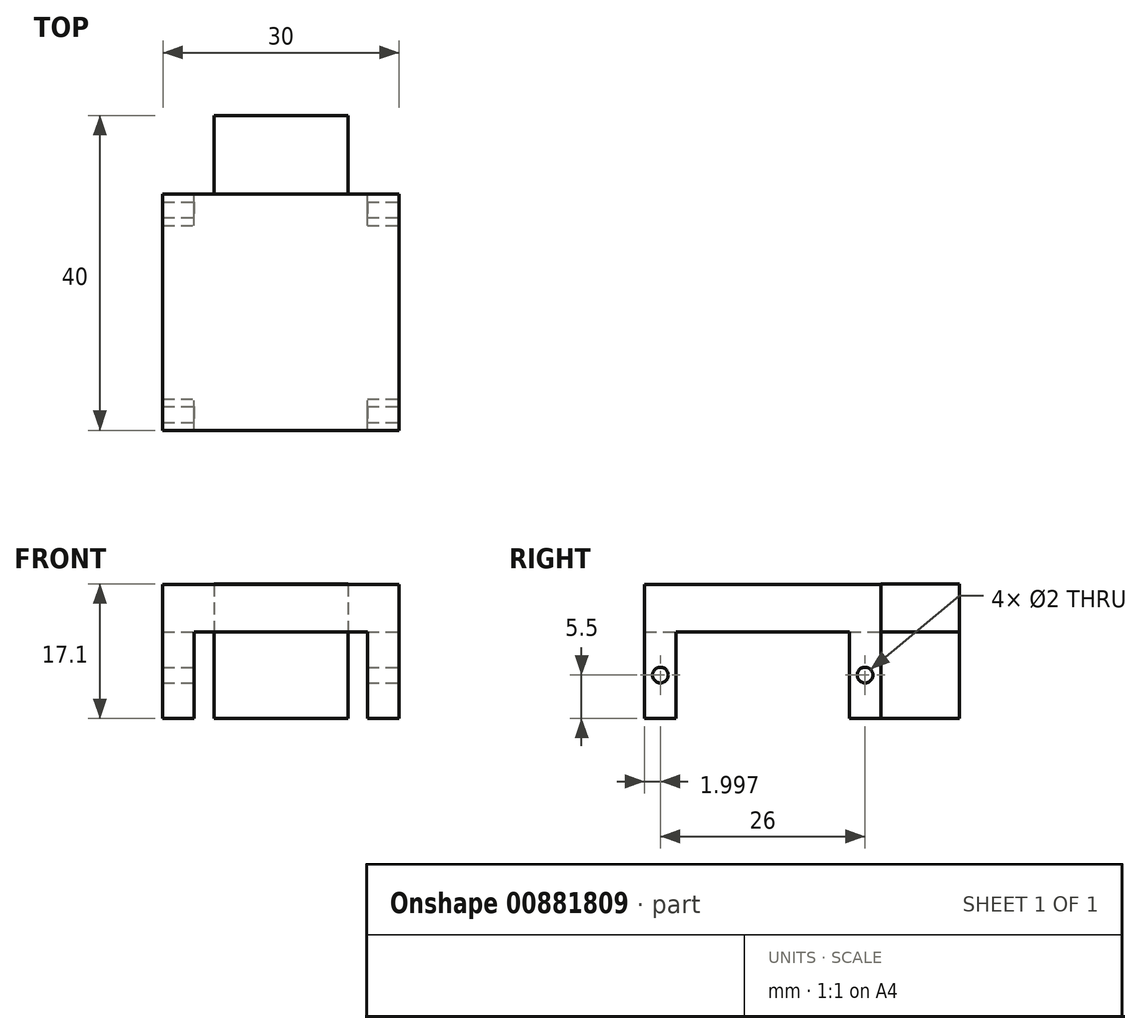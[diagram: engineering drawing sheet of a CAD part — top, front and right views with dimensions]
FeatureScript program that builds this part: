
annotation { "Feature Type Name" : "Feature", "Feature Type Description" : "" }
export const myFeature = defineFeature(function(context is Context, id is Id, definition is map)
    precondition{}
    {
        {
            var Q0;
            Q0=qCreatedBy(makeId("Top.planeOp"),FACE);
            var sketch = newSketch(context, id + "F0", { "sketchPlane" : qUnion([Q0])});
            skLineSegment(sketch, "E0.bottom", {"start": v(-18.4, 12.33) * mm, "end": v(11.6, 12.33) * mm});
            skLineSegment(sketch, "E0.top", {"start": v(-18.4, -17.67) * mm, "end": v(11.6, -17.67) * mm});
            skLineSegment(sketch, "E0.left", {"start": v(-18.4, 12.33) * mm, "end": v(-18.4, -17.67) * mm});
            skLineSegment(sketch, "E0.right", {"start": v(11.6, 12.33) * mm, "end": v(11.6, -17.67) * mm});
            skSolve(sketch);
        }
        {
            var Q0;
            Q0 = qSketchRegion(id + "F0", true);
            extrude(context, id + "F1", {"entities" : qUnion([Q0]), "depth" : 6 * mm, "offsetDistance" : 25 * mm});
        }
        {
            var Q0;
            Q0=makeQuery(id+"F1.opExtrude","CAP_FACE",FACE,{"disambiguationData":[OSD([sQuery(id+"F0.wireOp",EDGE,"E0.bottom"),sQuery(id+"F0.wireOp",EDGE,"E0.top"),sQuery(id+"F0.wireOp",EDGE,"E0.left"),sQuery(id+"F0.wireOp",EDGE,"E0.right")])],"isStart":true});
            var sketch = newSketch(context, id + "F2", { "sketchPlane" : qUnion([Q0])});
            skLineSegment(sketch, "E1.bottom", {"start": v(-18.4, 17.67) * mm, "end": v(-14.4, 17.67) * mm});
            skLineSegment(sketch, "E1.top", {"start": v(-18.4, 13.67) * mm, "end": v(-14.4, 13.67) * mm});
            skLineSegment(sketch, "E1.left", {"start": v(-18.4, 17.67) * mm, "end": v(-18.4, 13.67) * mm});
            skLineSegment(sketch, "E1.right", {"start": v(-14.4, 17.67) * mm, "end": v(-14.4, 13.67) * mm});
            skPoint(sketch, "E2", {"position": v(7.6, 17.67) * mm});
            skLineSegment(sketch, "E3", {"start": v(7.6, 17.67) * mm, "end": v(7.6, 13.67) * mm});
            skPoint(sketch, "E4", {"position": v(-18.4, -8.33) * mm});
            skLineSegment(sketch, "E5", {"start": v(-18.4, -8.33) * mm, "end": v(-14.4, -8.33) * mm});
            skPoint(sketch, "E6", {"position": v(-14.4, 13.67) * mm});
            skPoint(sketch, "E7", {"position": v(7.6, 13.67) * mm});
            skPoint(sketch, "E8", {"position": v(-14.4, -8.33) * mm});
            skPoint(sketch, "E9", {"position": v(7.6, -8.33) * mm});
            skLineSegment(sketch, "E10.trimOffspring", {"start": v(7.6, 13.67) * mm, "end": v(11.6, 13.67) * mm});
            skLineSegment(sketch, "E11.trimOffspring", {"start": v(7.6, -8.33) * mm, "end": v(11.6, -8.33) * mm});
            skLineSegment(sketch, "E12.trimOffspring", {"start": v(-14.4, -8.33) * mm, "end": v(-14.4, -12.33) * mm});
            skLineSegment(sketch, "E13.trimOffspring", {"start": v(7.6, -8.33) * mm, "end": v(7.6, -12.33) * mm});
            skLineSegment(sketch, "E14.bottom", {"start": v(-11.9, -12.33) * mm, "end": v(5.1, -12.33) * mm});
            skLineSegment(sketch, "E14.top", {"start": v(-11.9, -22.33) * mm, "end": v(5.1, -22.33) * mm});
            skLineSegment(sketch, "E14.left", {"start": v(-11.9, -12.33) * mm, "end": v(-11.9, -22.33) * mm});
            skLineSegment(sketch, "E14.right", {"start": v(5.1, -12.33) * mm, "end": v(5.1, -22.33) * mm});
            skSolve(sketch);
        }
        {
            var Q0;
            Q0 = qSketchRegion(id + "F2", true);
            var Q1;
            {var subQ0=sQuery(id+"F2.wireOp",EDGE,"E3");Q1=makeQuery(id+"F2.imprint","IMPRINT",FACE,{"disambiguationData":[TD([[makeQuery(id+"F2.imprint","IMPRINT",EDGE,{"derivedFrom":subQ0}),1.0]])]});}
            var Q2;
            {var subQ0=sQuery(id+"F2.wireOp",EDGE,"E5");Q2=makeQuery(id+"F2.imprint","IMPRINT",FACE,{"disambiguationData":[TD([[makeQuery(id+"F2.imprint","IMPRINT",EDGE,{"derivedFrom":subQ0}),-1.0]])]});}
            var Q3;
            {var subQ0=sQuery(id+"F2.wireOp",EDGE,"E11.trimOffspring");Q3=makeQuery(id+"F2.imprint","IMPRINT",FACE,{"disambiguationData":[TD([[makeQuery(id+"F2.imprint","IMPRINT",EDGE,{"derivedFrom":subQ0}),-1.0]])]});}
            extrude(context, id + "F3", {"entities" : qUnion([Q0, Q1, Q2, Q3]), "operationType" : NewBodyOperationType.ADD, "depth" : 11 * mm, "offsetDistance" : 25 * mm});
        }
        {
            var Q0;
            {var subQ0=sQuery(id+"F0.wireOp",EDGE,"E0.right");var subQ1=makeQuery(id+"F1.opExtrude","CAP_EDGE",EDGE,{"disambiguationData":[OSD([subQ0])],"isStart":true});Q0=makeQuery(id+"F3.boolean.opBoolean","MERGE",FACE,{"derivedFrom":[makeQuery(id+"F1.opExtrude","SWEPT_FACE",FACE,{"disambiguationData":[OSD([subQ0])]}),makeQuery(id+"F3.opExtrude","SWEPT_FACE",FACE,{"disambiguationData":[OSD([subQ0]),TDD([makeQuery(id+"F2.imprint","IMPRINT",EDGE,{"disambiguationData":[TD([[makeQuery(id+"F2.imprint","INTERSECT",VERTEX,{"derivedFrom":[makeQuery(id+"F1.opExtrude","CAP_EDGE",EDGE,{"disambiguationData":[OSD([sQuery(id+"F0.wireOp",EDGE,"E0.bottom")])],"isStart":true}),subQ1]}),-1.0]])],"derivedFrom":subQ1})])]}),makeQuery(id+"F3.opExtrude","SWEPT_FACE",FACE,{"disambiguationData":[OSD([subQ0]),TDD([makeQuery(id+"F2.imprint","IMPRINT",EDGE,{"disambiguationData":[TD([[makeQuery(id+"F2.imprint","INTERSECT",VERTEX,{"derivedFrom":[makeQuery(id+"F1.opExtrude","CAP_EDGE",EDGE,{"disambiguationData":[OSD([sQuery(id+"F0.wireOp",EDGE,"E0.top")])],"isStart":true}),subQ1]}),1.0]])],"derivedFrom":subQ1})])]})]});}
            var sketch = newSketch(context, id + "F4", { "sketchPlane" : qUnion([Q0])});
            skLineSegment(sketch, "E15", {"start": v(-17.67, 0) * mm, "end": v(-13.67, -11) * mm});
            skLineSegment(sketch, "E16", {"start": v(-13.67, -11) * mm, "end": v(-17.67, -11) * mm});
            skLineSegment(sketch, "E17", {"start": v(-17.67, -11) * mm, "end": v(-13.67, 0) * mm});
            skLineSegment(sketch, "E18", {"start": v(8.33, 0) * mm, "end": v(12.33, -11) * mm});
            skLineSegment(sketch, "E19", {"start": v(12.33, -11) * mm, "end": v(12.33, 0) * mm});
            skLineSegment(sketch, "E20", {"start": v(12.33, 0) * mm, "end": v(8.33, -11) * mm});
            skPoint(sketch, "E21", {"position": v(-15.67, -5.5) * mm});
            skPoint(sketch, "E22", {"position": v(10.33, -5.5) * mm});
            skSolve(sketch);
        }
        {
            var Q0;
            Q0=sQuery(id+"F4.wireOp",VERTEX,"E21");
            var Q1;
            Q1=sQuery(id+"F4.wireOp",VERTEX,"E22");
            var Q2;
            Q2=makeQuery(id+"F1.opExtrude","SWEPT_BODY",BODY,{"disambiguationData":[OSD([sQuery(id+"F0.wireOp",EDGE,"E0.bottom"),sQuery(id+"F0.wireOp",EDGE,"E0.top"),sQuery(id+"F0.wireOp",EDGE,"E0.left"),sQuery(id+"F0.wireOp",EDGE,"E0.right")])]});
            hole(context, id + "F5", {"style" : HoleStyle.SIMPLE, "endStyle" : HoleEndStyle.THROUGH, "holeDiameter" : 2 * mm, "majorDiameter" : 5 * mm, "isTappedThrough" : true, "tappedDepth" : 12 * mm, "tapClearance" : 3, "locations" : qUnion([Q0, Q1]), "scope" : qUnion([Q2])});
        }
        {
            var Q0;
            Q0=makeQuery(id+"F3.opExtrude","CAP_FACE",FACE,{"disambiguationData":[OSD([sQuery(id+"F2.wireOp",EDGE,"E14.bottom"),sQuery(id+"F2.wireOp",EDGE,"E14.top"),sQuery(id+"F2.wireOp",EDGE,"E14.left"),sQuery(id+"F2.wireOp",EDGE,"E14.right")])],"isStart":false});
            extrude(context, id + "F6", {"entities" : qUnion([Q0]), "oppositeDirection" : true, "depth" : 17.1 * mm, "offsetDistance" : 25 * mm});
        }
    });
